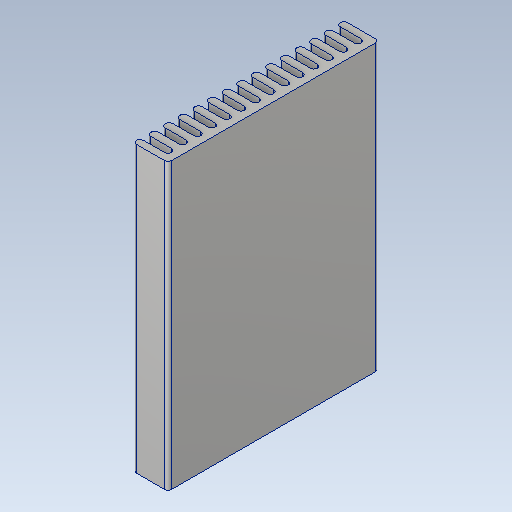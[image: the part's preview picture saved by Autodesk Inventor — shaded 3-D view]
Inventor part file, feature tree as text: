
AUTODESK INVENTOR PART (.ipt)
format: ipt  version: 2020 (Build 240168000, 168)  size: 278,016 bytes
history: native  units: mm
features: fillet x7, other x2, extrude x2, sketch x2, pattern_linear x1
ambient origin geometry x8: Origin, YZ Plane, XZ Plane, XY Plane, X Axis, Y Axis, Z Axis, Center Point
bodies: Body1 (feature_tree)
feature tree (14):
  other  "Bryła1"
  extrude  "Wyciągnięcie proste1"  Depth=10.0mm
  extrude  "Wyciągnięcie proste2"  Depth=5.0mm
  pattern_linear  "Szyk prostokątny1"  Count1=6  [1 undecoded]
  fillet  "Zaokrąglenie1"  Radius=30.0mm
  fillet  "Zaokrąglenie2"  Radius=100.0mm
  fillet  "Zaokrąglenie3"  Radius=2.0mm
  fillet  "Zaokrąglenie4"  Radius=2.0mm
  fillet  "Zaokrąglenie5"  Radius=2.0mm
  fillet  "Zaokrąglenie6"  Radius=100.0mm
  fillet  "Zaokrąglenie7"  Radius=4.15mm
  other  "Pogrubienie1"
  sketch  "Szkic1"
  sketch  "Szkic2"
note: 1 required parameter value undecoded (feature->parameter linkage not recoverable at this tier; creation-order binding heuristic only, values carry confidence <= 0.55)
